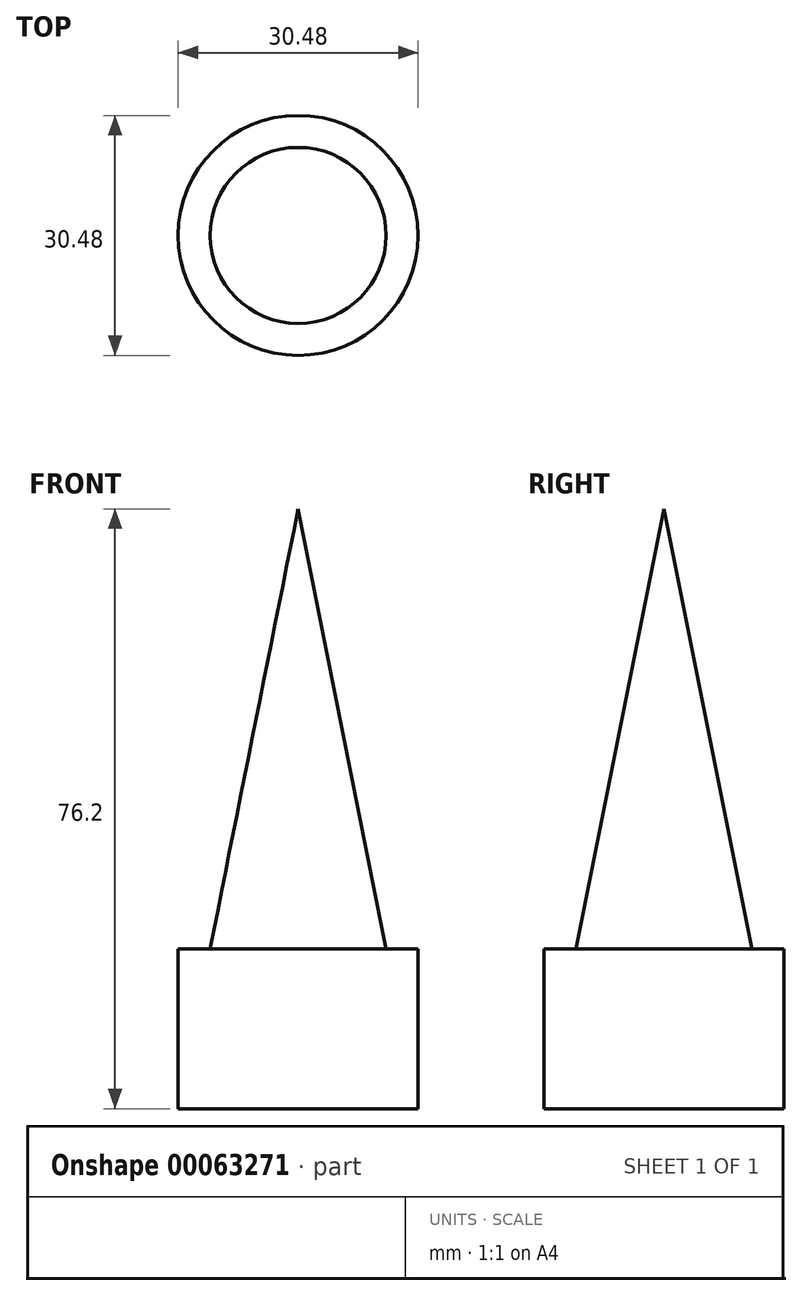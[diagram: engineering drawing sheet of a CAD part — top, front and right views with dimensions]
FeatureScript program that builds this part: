
annotation { "Feature Type Name" : "Feature", "Feature Type Description" : "" }
export const myFeature = defineFeature(function(context is Context, id is Id, definition is map)
    precondition{}
    {
        {
            var Q0;
            Q0=qCreatedBy(makeId("Top.planeOp"),FACE);
            var sketch = newSketch(context, id + "F0", { "sketchPlane" : qUnion([Q0])});
            skCircle(sketch, "E0", {"center": v(0, 0) * mm, "radius": 15.24 * mm});
            skSolve(sketch);
        }
        {
            var Q0;
            Q0=qCreatedBy(makeId("Front.planeOp"),FACE);
            var sketch = newSketch(context, id + "F1", { "sketchPlane" : qUnion([Q0])});
            skLineSegment(sketch, "E1", {"start": v(0, 0) * mm, "end": v(-15.24, 0) * mm});
            skLineSegment(sketch, "E2", {"start": v(-15.24, 0) * mm, "end": v(0, 76.2) * mm});
            skLineSegment(sketch, "E3", {"start": v(0, 76.2) * mm, "end": v(0, 0) * mm});
            skSolve(sketch);
        }
        {
            var Q0;
            Q0 = qSketchRegion(id + "F1", true);
            var Q1;
            Q1=sQuery(id+"F1.wireOp",EDGE,"E3");
            revolve(context, id + "F2", {"entities" : qUnion([Q0]), "axis" : qUnion([Q1]), "revolveType" : RevolveType.FULL});
        }
        {
            var Q0;
            Q0 = qSketchRegion(id + "F0", true);
            extrude(context, id + "F3", {"entities" : qUnion([Q0]), "operationType" : NewBodyOperationType.ADD, "depth" : 20.32 * mm});
        }
    });
